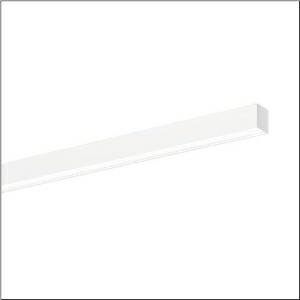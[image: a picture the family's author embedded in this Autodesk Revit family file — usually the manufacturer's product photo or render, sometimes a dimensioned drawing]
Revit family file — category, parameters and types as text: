
# Revit family: silica_21_51mx23db45wb
name_source: partatom
category: Lighting Fixtures
units: mm (PartAtom-declared; Revit-internal decimal feet)

## family parameters
Cut with Voids When Loaded = No
Host = Face
Light Source = No
Part Type = Normal
Room Calculation Point = No
Round Connector Dimension = Use Diameter
Shared = No

## types (1)
- --- (1 x LED, 4100 lm, 28.1 W, 4000K)
    Apparent Load = 28 VA
    CIE Flux Codes = 78 96 99 100 100
    Color Rendering = 80
    Color Temperature = 4000K
    Default Elevation = 1800 mm
    Description = Silica 21, office luminaire, primary optical cover: prismatic diffuser, of PMMA, CAT 2 (L<= 3000cd/m²), light emission: direct distribution, primary light characteristic: symmetric, installation type: surface-mounted, LED, rated luminous flux: 4.100lm, luminous efficacy: 146lm/W, light colour: 840, colour temperature: 4000K, control gear: DALI 2, with terminal, 3+2-pole, max. 2.5mm², mains connection: 220..240V, AC, 50/60Hz, rated input power: 28.1W, luminaire housing, of aluminium, traffic white (RAL 9016), length: 1.504mm, width: 53mm, height: 53mm, protection rating (complete): IP20, insulation class (complete): insulation class I (protective earthing), certification: CE, permissible operating ambient temperature: 0..+35°C, standard: EN 50419, packaging unit: 1 piece
    Height = 53 mm
    Lamp = 1 x LED
    Lamp Light Flux = 4100 lm
    Lamp Power = 28.1 W
    Lamp count = 1
    Length = 1504 mm
    Luminous efficacy = 146 lm/W
    Manufacturer = Siteco
    ModVariant = No
    Model = 51MX23DB45WB
    Mounting Place = Ceiling
    Mounting Type = Surface mounted
    Number of Poles = 1
    OnlyDefault = Yes
    Power Factor = 1
    Product Name = Silica 21
    Product group = office luminaire | ceiling mounted
    ProductGroupID = 301
    Protection Class = Protection class I
    Protection Degree = IP 20
    RLX_Detail_Level = 1
    RLX_Emergency_Light_Flux = 0 lm
    RLX_Emergency_Type = 0
    RLX_Emergency_Type_DB = No
    RlxData = <blob elided: 18881 chars, md5=e12f554f>
    Socket = socket
    Standby Power = 0 W
    System Light Flux = 4100 lm
    System Power = 28 W
    Type Comments = factory setting: luminous flux: 100 % | dim-lin: 254 | 323 mA
    Type Image = l_1335877.jpg
    URL = http://relux.com
    VarID = @adj_119757
    Voltage = 0 V
    Weight = 0.00 kg
    Width = 53 mm

## geometry (parser evidence)
native form markers: Blend x4, Sweep x13
no freeform markers — native parametric forms only
